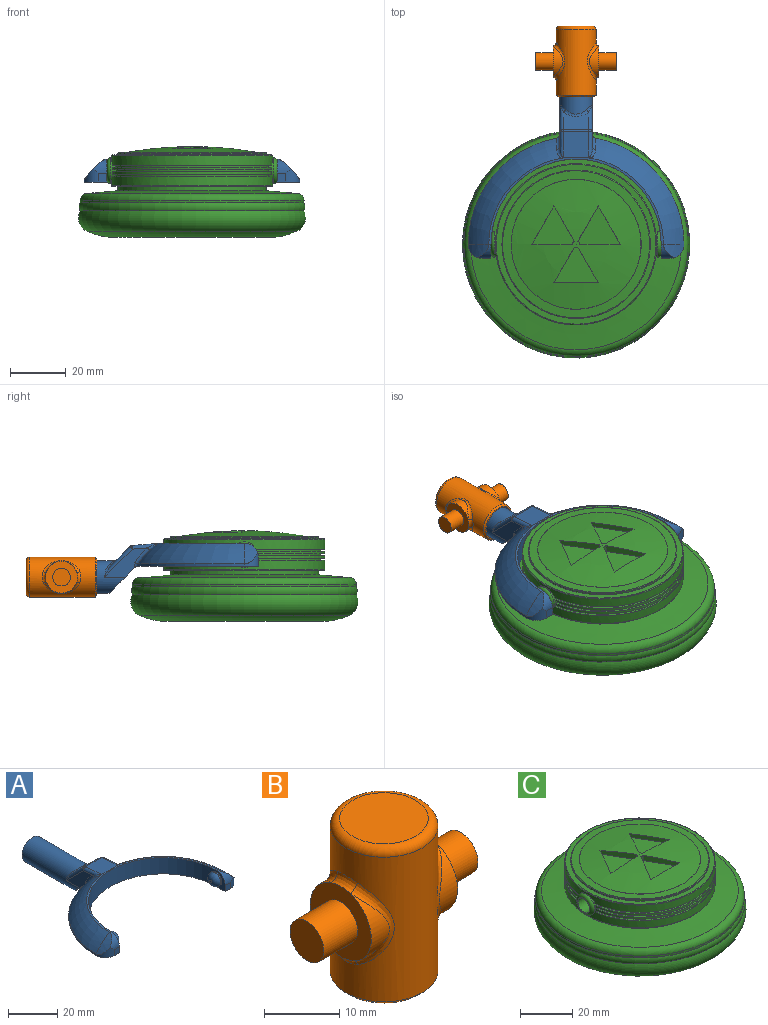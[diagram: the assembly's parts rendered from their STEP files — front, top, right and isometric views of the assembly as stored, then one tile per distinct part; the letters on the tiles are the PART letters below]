
ASSEMBLY  parts=3 mates=2
PART A: 48 faces, bbox 77.3x80.8x18.2 mm
  f0: plane 11.99x9.83mm, normal (0,-0.71,-0.71), area 141.5mm2, adj f1,f2,f9,f30,f43,f46
  f1: plane 15.39x10.49mm, normal (-1,0,0), area 63.5mm2, adj f0,f30,f32,f36,f46,f47
  f2: plane 15.39x10.49mm, normal (1,0,0), area 63.5mm2, adj f0,f30,f34,f39,f43,f44
  f3: plane 9.14x6.37mm, normal (0,0.71,0.71), area 67.6mm2, adj f35,f36,f39,f40
  f4: cylinder r=38.61mm len=37.99mm, axis (0,0,-1), area 42.6mm2, adj f6,f9,f17,f46,f47
  f5: torus R=19.3mm, axis (0,0,-1), area 507.8mm2, adj f10,f11,f12,f29,f42,f44
  f6: torus R=19.3mm, axis (0,0,-1), area 507.8mm2, adj f4,f11,f15,f28,f45,f47
  f7: cylinder r=30.48mm len=60.96mm, axis (0,0,-1), area 746.6mm2, adj f8,f9,f11,f14,f21,f24
  f8: plane 8.13x5.08mm, normal (-1,0,0), area 19.9mm2, adj f7,f9,f13,f19,f24
  f9: plane 77.22x43.73mm, normal (0,0,-1), area 956.2mm2, adj f0,f4,f7,f8,f10,f13,f14,f16
  f10: cylinder r=38.61mm len=37.99mm, axis (0,0,-1), area 42.6mm2, adj f5,f9,f20,f43,f44
  f11: plane 62.55x30.95mm, normal (0,0,1), area 75mm2, adj f5,f6,f7,f18,f19,f27
  f12: cylinder r=22.71mm len=7.33mm, axis (0,1,0), area 24.8mm2, adj f5,f19,f20
  f13: plane 3.05x3.05mm, normal (0,-1,0), area 9.3mm2, adj f8,f9,f19,f20
  f14: plane 8.13x5.08mm, normal (1,0,0), area 19.9mm2, adj f7,f9,f16,f18,f21
  f15: cylinder r=22.71mm len=7.33mm, axis (0,1,0), area 24.8mm2, adj f6,f17,f18
  f16: plane 3.05x3.05mm, normal (0,-1,0), area 9.3mm2, adj f9,f14,f17,f18
  f17: cylinder r=5.08mm len=5.08mm, axis (0,0,-1), area 21.9mm2, adj f4,f9,f15,f16,f18
  f18: cylinder r=5.08mm len=5.08mm, axis (-1,0,0), area 21.9mm2, adj f11,f14,f15,f16,f17
  f19: cylinder r=5.08mm len=5.08mm, axis (-1,0,0), area 21.9mm2, adj f8,f11,f12,f13,f20
  f20: cylinder r=5.08mm len=5.08mm, axis (0,0,-1), area 21.9mm2, adj f9,f10,f12,f13,f19
  f21: cylinder r=3.17mm len=6.35mm, axis (-1,0,0), area 12.7mm2, adj f7,f14,f23
  f22: plane 1.27x1.27mm, normal (1,0,0), area 1.3mm2, adj f23
  f23: torus R=0.64mm, axis (1,0,0), area 56.5mm2, adj f21,f22
  f24: cylinder r=3.17mm len=6.35mm, axis (1,0,0), area 12.7mm2, adj f7,f8,f26
  f25: plane 1.27x1.27mm, normal (-1,0,0), area 1.3mm2, adj f26
  f26: torus R=0.64mm, axis (-1,0,0), area 56.5mm2, adj f24,f25
  f27: plane 9.86x9.36mm, normal (0,0.09,1), area 85.6mm2, adj f11,f28,f29,f32,f34,f35,f42,f45
  f28: plane 1.04x0.17mm, normal (0,-1,0), area 0mm2, adj f6,f27,f45
  f29: plane 1.04x0.17mm, normal (0,-1,0), area 0mm2, adj f5,f27,f42
  f30: cylinder r=5.84mm len=33.01mm, axis (0,-1,0), area 1029.7mm2, adj f0,f1,f2,f31,f38,f40,f41
  f31: plane 11.68x11.68mm, normal (0,1,0), area 107.2mm2, adj f30
  f32: cylinder r=1.27mm len=9.13mm, axis (0,-1,0.09), area 14.4mm2, adj f1,f27,f33,f45
  f33: sphere r=1.27mm, area 1.5mm2, adj f32,f35,f36
  f34: cylinder r=1.27mm len=9.13mm, axis (0,1,-0.09), area 14.4mm2, adj f2,f27,f37,f42
  f35: cylinder r=1.27mm len=9.14mm, axis (-1,0,0), area 8.1mm2, adj f3,f27,f33,f37
  f36: cylinder r=1.27mm len=10.91mm, axis (0,-0.71,0.71), area 23.1mm2, adj f1,f3,f33,f38
  f37: sphere r=1.27mm, area 1.5mm2, adj f34,f35,f39
  f38: bspline ~4.55x2.75mm, area 2.3mm2, adj f30,f36,f40
  f39: cylinder r=1.27mm len=10.91mm, axis (0,0.71,-0.71), area 23.1mm2, adj f2,f3,f37,f41
  f40: bspline ~9.14x2.56mm, area 10.7mm2, adj f3,f30,f38,f41
  f41: bspline ~5.23x3.53mm, area 2.3mm2, adj f30,f39,f40
  f42: bspline ~4.62x3.14mm, area 5.2mm2, adj f5,f27,f29,f34,f44
  f43: cylinder r=1.27mm len=1.74mm, axis (0,0,-1), area 1.9mm2, adj f0,f2,f9,f10,f44
  f44: bspline ~8.6x7.86mm, area 11.9mm2, adj f2,f5,f10,f42,f43
  f45: bspline ~4.62x3.14mm, area 5.2mm2, adj f6,f27,f28,f32,f47
  f46: cylinder r=1.27mm len=1.74mm, axis (0,0,-1), area 1.9mm2, adj f0,f1,f4,f9,f47
  f47: bspline ~8.6x7.86mm, area 11.9mm2, adj f1,f4,f6,f45,f46
PART B: 25 faces, bbox 28.9x15.5x25.4 mm
  f0: cylinder r=5.71mm len=10.81mm, axis (-1,0,0), area 26.2mm2, adj f5,f15
  f1: cylinder r=5.71mm len=10.81mm, axis (-1,0,0), area 26.2mm2, adj f8,f11
  f2: cylinder r=7.14mm len=23.5mm, axis (0,0,-1), area 763.2mm2, adj f9,f10,f11,f12,f13,f14,f15,f16
  f3: plane 11.75x11.75mm, normal (0,0,1), area 108.4mm2, adj f17
  f4: plane 13.02x13.02mm, normal (0,0,-1), area 16.3mm2, adj f22,f24
  f5: plane 11.46x11.46mm, normal (1,0,0), area 70.9mm2, adj f0,f6,f13,f16,f18
  f6: cylinder r=5.71mm len=10.81mm, axis (-1,0,0), area 26.2mm2, adj f5,f14
  f7: cylinder r=5.71mm len=10.81mm, axis (-1,0,0), area 26.2mm2, adj f8,f10
  f8: plane 11.46x11.46mm, normal (-1,0,0), area 70.9mm2, adj f1,f7,f9,f12,f20
  f9: bspline ~4.64x1.73mm, area 6.5mm2, adj f2,f8,f10,f11
  f10: bspline ~13.62x4.91mm, area 20.7mm2, adj f2,f7,f9,f12
  f11: bspline ~13.6x4.87mm, area 20.7mm2, adj f1,f2,f9,f12
  f12: bspline ~4.64x1.73mm, area 6.5mm2, adj f2,f8,f10,f11
  f13: bspline ~4.64x1.73mm, area 6.5mm2, adj f2,f5,f14,f15
  f14: bspline ~13.62x4.91mm, area 20.7mm2, adj f2,f6,f13,f16
  f15: bspline ~13.6x4.87mm, area 20.7mm2, adj f0,f2,f13,f16
  f16: bspline ~4.64x1.73mm, area 6.5mm2, adj f2,f5,f14,f15
  f17: torus R=5.87mm, axis (0,0,1), area 83.8mm2, adj f2,f3
  f18: cylinder r=3.17mm len=6.35mm, axis (-1,0,0), area 126.7mm2, adj f5,f19
  f19: plane 6.35x6.35mm, normal (1,0,0), area 31.7mm2, adj f18
  f20: cylinder r=3.17mm len=6.35mm, axis (1,0,0), area 126.7mm2, adj f8,f21
  f21: plane 6.35x6.35mm, normal (-1,0,0), area 31.7mm2, adj f20
  f22: cylinder r=6.1mm len=22.86mm, axis (0,0,-1), area 875.6mm2, adj f4,f23
  f23: plane 12.19x12.19mm, normal (0,0,-1), area 116.7mm2, adj f22
  f24: cone r=7.14mm half-angle=45deg, axis (0,0,1), area 38.5mm2, adj f2,f4
PART C: 64 faces, bbox 96.3x96.3x32.5 mm
  f0: cylinder r=28.87mm len=57.73mm, axis (0,0,-1), area 595.7mm2, adj f3,f4,f54,f55,f60
  f1: plane 57.18x24.54mm, normal (0,0,-1), area 101.5mm2, adj f6,f8,f54,f55
  f2: plane 57.18x24.54mm, normal (0,0,-1), area 101.4mm2, adj f5,f7,f54,f55
  f3: plane 57.14x24.72mm, normal (0,0,1), area 102.1mm2, adj f0,f5,f54,f55
  f4: plane 57.14x24.72mm, normal (0,0,1), area 102mm2, adj f0,f6,f54,f55
  f5: cylinder r=27.6mm len=54.57mm, axis (0,0,-1), area 49.6mm2, adj f2,f3,f54,f55
  f6: cylinder r=27.6mm len=54.57mm, axis (0,0,-1), area 49.6mm2, adj f1,f4,f54,f55
  f7: cylinder r=28.87mm len=57.06mm, axis (0,0,-1), area 77.8mm2, adj f2,f12,f54,f55
  f8: cylinder r=28.87mm len=57.06mm, axis (0,0,-1), area 77.8mm2, adj f1,f11,f54,f55
  f9: plane 57.12x24.37mm, normal (0,0,-1), area 101mm2, adj f13,f15,f54,f55
  f10: plane 57.12x24.37mm, normal (0,0,-1), area 101mm2, adj f14,f16,f54,f55
  f11: plane 57.02x24.31mm, normal (0,0,1), area 101mm2, adj f8,f14,f54,f55
  f12: plane 57.02x24.31mm, normal (0,0,1), area 101mm2, adj f7,f13,f54,f55
  f13: cylinder r=27.6mm len=54.44mm, axis (0,0,-1), area 49.2mm2, adj f9,f12,f54,f55
  f14: cylinder r=27.6mm len=54.44mm, axis (0,0,-1), area 49.2mm2, adj f10,f11,f54,f55
  f15: cylinder r=28.87mm len=57.06mm, axis (0,0,-1), area 77.8mm2, adj f9,f19,f54,f55
  f16: cylinder r=28.87mm len=57.06mm, axis (0,0,-1), area 77.8mm2, adj f10,f20,f54,f55
  f17: plane 57.25x24.77mm, normal (0,0,-1), area 102mm2, adj f22,f23,f54,f55
  f18: plane 57.25x24.77mm, normal (0,0,-1), area 102.1mm2, adj f21,f23,f54,f55
  f19: plane 57.07x24.48mm, normal (0,0,1), area 101.4mm2, adj f15,f21,f54,f55
  f20: plane 57.07x24.48mm, normal (0,0,1), area 101.5mm2, adj f16,f22,f54,f55
  f21: cylinder r=27.6mm len=54.57mm, axis (0,0,-1), area 49.6mm2, adj f18,f19,f54,f55
  f22: cylinder r=27.6mm len=54.57mm, axis (0,0,-1), area 49.6mm2, adj f17,f20,f54,f55
  f23: cylinder r=28.87mm len=57.73mm, axis (0,0,-1), area 595.8mm2, adj f17,f18,f54,f55,f61
  f24: sphere r=135.39mm, area 1385.3mm2, adj f38,f39,f40,f41,f43,f44,f45,f46
  f25: plane 39.35x39.35mm, normal (0,0,-1), area 1216.2mm2, adj f26
  f26: torus R=20.13mm, axis (0,0,-1), area 1430.4mm2, adj f25,f27
  f27: torus R=27.75mm, axis (0,0,-1), area 3543.7mm2, adj f26,f28
  f28: torus R=35.37mm, axis (0,0,-1), area 2180.8mm2, adj f27,f29
  f29: torus R=37.36mm, axis (0,0,-1), area 734.8mm2, adj f28,f30
  f30: cylinder r=40.07mm len=80.14mm, axis (0,0,-1), area 213.4mm2, adj f29,f34
  f31: cone r=26.58mm half-angle=85deg, axis (0,0,-1), area 2265.9mm2, adj f32,f34
  f32: cylinder r=26.58mm len=53.16mm, axis (0,0,-1), area 265.1mm2, adj f31,f33
  f33: plane 57.23x57.23mm, normal (0,0,-1), area 352.3mm2, adj f32,f60
  f34: torus R=37.53mm, axis (0,0,1), area 928.9mm2, adj f30,f31
  f35: cone r=26.58mm half-angle=87deg, axis (0,0,-1), area 477.5mm2, adj f62,f63
  f36: cylinder r=26.58mm len=53.16mm, axis (0,0,-1), area 92.3mm2, adj f37,f62
  f37: plane 57.23x57.23mm, normal (0,0,1), area 352.3mm2, adj f36,f61
  f38: plane 14.61x2.53mm, normal (0,1,0), area 32.2mm2, adj f24,f39,f41,f42
  f39: cylinder r=1.27mm len=2.53mm, axis (0,0,1), area 3.4mm2, adj f24,f38,f40,f42
  f40: plane 12.65x7.3mm, normal (-0.87,-0.5,0), area 32.2mm2, adj f24,f39,f41,f42
  f41: plane 13.75x7.94mm, normal (0.87,-0.5,0), area 28mm2, adj f24,f38,f40,f42
  f42: plane 15.24x13.75mm, normal (0,0,1), area 108.3mm2, adj f38,f39,f40,f41
  f43: plane 12.65x7.3mm, normal (0.87,-0.5,0), area 32.2mm2, adj f24,f44,f46,f47
  f44: plane 15.88x1.84mm, normal (0,1,0), area 28mm2, adj f24,f43,f45,f47
  f45: plane 12.65x7.3mm, normal (-0.87,-0.5,0), area 32.2mm2, adj f24,f44,f46,f47
  f46: cylinder r=1.27mm len=2.53mm, axis (0,0,1), area 3.4mm2, adj f24,f43,f45,f47
  f47: plane 15.88x12.65mm, normal (0,0,1), area 108.3mm2, adj f43,f44,f45,f46
  f48: plane 12.65x7.3mm, normal (0.87,-0.5,0), area 32.2mm2, adj f24,f49,f51,f52
  f49: cylinder r=1.27mm len=2.53mm, axis (0,0,1), area 3.4mm2, adj f24,f48,f50,f52
  f50: plane 14.61x2.53mm, normal (0,1,0), area 32.2mm2, adj f24,f49,f51,f52
  f51: plane 13.75x7.94mm, normal (-0.87,-0.5,0), area 28mm2, adj f24,f48,f50,f52
  f52: plane 15.24x13.75mm, normal (0,0,1), area 108.3mm2, adj f48,f49,f50,f51
  f53: plane 6.6x6.6mm, normal (1,0,0), area 2.6mm2, adj f58,f59
  f54: cylinder r=4.57mm len=9.14mm, axis (-1,0,0), area 23.9mm2, adj f0,f1,f2,f3,f4,f5,f6,f7
  f55: cylinder r=4.57mm len=9.14mm, axis (-1,0,0), area 20.2mm2, adj f0,f1,f2,f3,f4,f5,f6,f7
  f56: plane 6.6x6.6mm, normal (-1,0,0), area 2.6mm2, adj f57,f59
  f57: torus R=3.3mm, axis (1,0,0), area 51.5mm2, adj f55,f56
  f58: torus R=3.3mm, axis (1,0,0), area 51.5mm2, adj f53,f54
  f59: cylinder r=3.17mm len=60.96mm, axis (1,0,0), area 1216.1mm2, adj f53,f56
  f60: torus R=28.61mm, axis (0,0,1), area 72.1mm2, adj f0,f33
  f61: torus R=28.61mm, axis (0,0,-1), area 72.1mm2, adj f23,f37
  f62: torus R=26.33mm, axis (0,0,1), area 64.2mm2, adj f35,f36
  f63: torus R=23.29mm, axis (0,0,1), area 4.5mm2, adj f24,f35
PLACE A t=(32.34,27.52,20.85)mm
PLACE B rot(axis=(-1,0,0),90deg) t=(32.34,80.3,16.88)mm
PLACE C t=(32.34,27.52,33.52)mm
MATE revolute A.f24 <-> C.f54  axis (-1,0,0) through (62.82,27.52,24.92)mm
MATE revolute B.f2 <-> A.f30  axis (0,-1,0) through (32.34,103.16,16.88)mm
